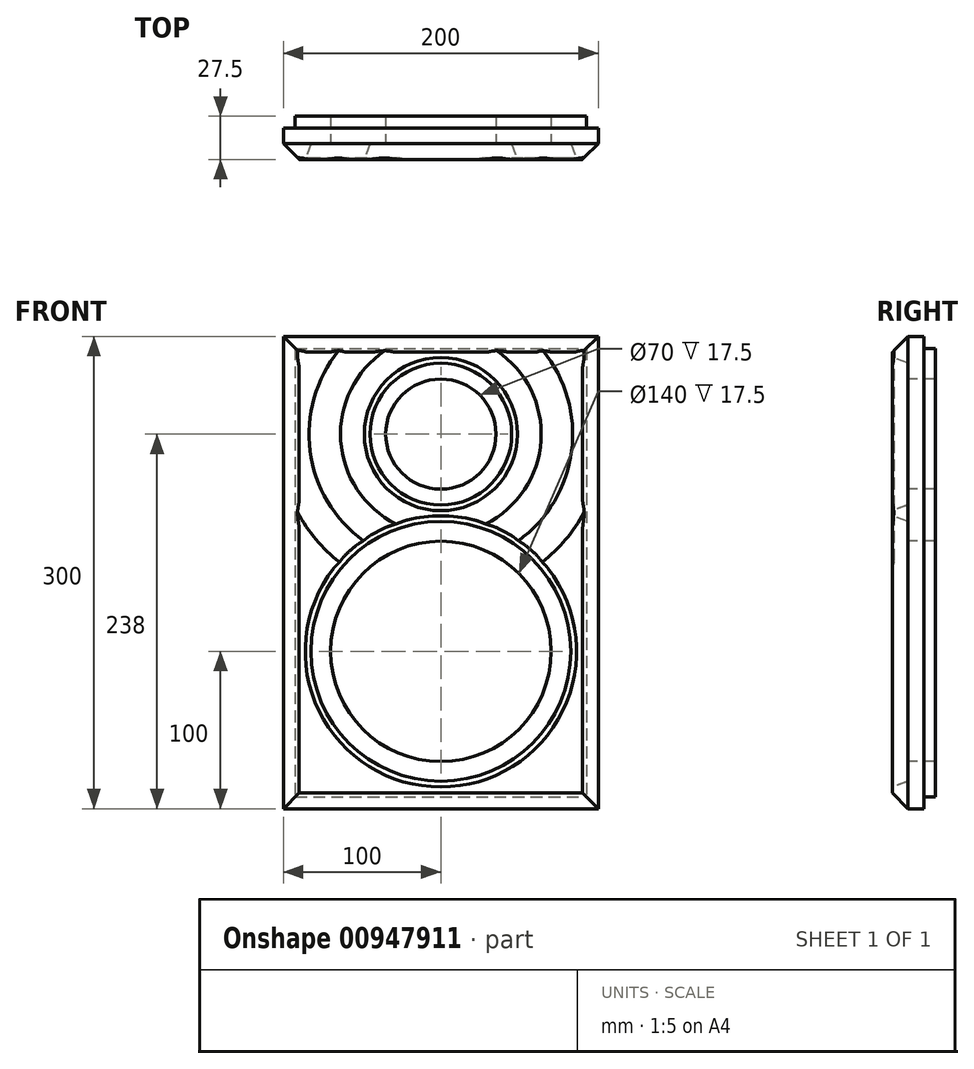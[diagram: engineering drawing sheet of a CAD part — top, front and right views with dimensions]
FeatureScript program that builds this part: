
annotation { "Feature Type Name" : "Feature", "Feature Type Description" : "" }
export const myFeature = defineFeature(function(context is Context, id is Id, definition is map)
    precondition{}
    {
        {
            var Q0;
            Q0=qCreatedBy(makeId("Right.planeOp"),FACE);
            cPlane(context, id + "F0", {"entities" : qUnion([Q0]), "cplaneType" : CPlaneType.OFFSET, "offset" : 100 * mm, "width" : 150 * mm, "height" : 150 * mm});
        }
        {
            var Q0;
            Q0=qCreatedBy(makeId("Right.planeOp"),FACE);
            cPlane(context, id + "F1", {"entities" : qUnion([Q0]), "cplaneType" : CPlaneType.OFFSET, "offset" : 100 * mm, "oppositeDirection" : true, "width" : 150 * mm, "height" : 150 * mm});
        }
        {
            var Q0;
            Q0=qCreatedBy(makeId("Right.planeOp"),FACE);
            cPlane(context, id + "F2", {"entities" : qUnion([Q0]), "cplaneType" : CPlaneType.OFFSET, "offset" : (100 - 7.5) * mm, "width" : 150 * mm, "height" : 150 * mm});
        }
        {
            var Q0;
            Q0=qCreatedBy(makeId("Right.planeOp"),FACE);
            cPlane(context, id + "F3", {"entities" : qUnion([Q0]), "cplaneType" : CPlaneType.OFFSET, "offset" : (100 - 7.5) * mm, "oppositeDirection" : true, "width" : 150 * mm, "height" : 150 * mm});
        }
        {
            var Q0;
            Q0=qCreatedBy(makeId("Top.planeOp"),FACE);
            cPlane(context, id + "F4", {"entities" : qUnion([Q0]), "cplaneType" : CPlaneType.OFFSET, "offset" : 7.7 * mm, "width" : 150 * mm, "height" : 150 * mm});
        }
        {
            var Q0;
            Q0=qCreatedBy(makeId("Top.planeOp"),FACE);
            cPlane(context, id + "F5", {"entities" : qUnion([Q0]), "cplaneType" : CPlaneType.OFFSET, "offset" : 300 * mm, "width" : 150 * mm, "height" : 150 * mm});
        }
        {
            var Q0;
            Q0=qCreatedBy(makeId("Top.planeOp"),FACE);
            cPlane(context, id + "F6", {"entities" : qUnion([Q0]), "cplaneType" : CPlaneType.OFFSET, "offset" : (300 - 7.5) * mm, "width" : 150 * mm, "height" : 150 * mm});
        }
        {
            var Q0;
            Q0=qCreatedBy(makeId("Front.planeOp"),FACE);
            cPlane(context, id + "F7", {"entities" : qUnion([Q0]), "cplaneType" : CPlaneType.OFFSET, "offset" : 150 * mm, "width" : 150 * mm, "height" : 150 * mm});
        }
        {
            var Q0;
            Q0=qCreatedBy(makeId("Front.planeOp"),FACE);
            cPlane(context, id + "F8", {"entities" : qUnion([Q0]), "cplaneType" : CPlaneType.OFFSET, "offset" : (150 - 7.5) * mm, "width" : 150 * mm, "height" : 150 * mm});
        }
        {
            var Q0;
            Q0=qCreatedBy(id+"F8.planeOp",FACE);
            var sketch = newSketch(context, id + "F9", { "sketchPlane" : qUnion([Q0])});
            skLineSegment(sketch, "E0.bottom", {"start": v(-92.5, 292.5) * mm, "end": v(92.5, 292.5) * mm});
            skLineSegment(sketch, "E0.top", {"start": v(-92.5, 7.7) * mm, "end": v(92.5, 7.7) * mm});
            skLineSegment(sketch, "E0.left", {"start": v(-92.5, 292.5) * mm, "end": v(-92.5, 7.7) * mm});
            skLineSegment(sketch, "E0.right", {"start": v(92.5, 292.5) * mm, "end": v(92.5, 7.7) * mm});
            skSolve(sketch);
        }
        {
            var Q0;
            Q0=makeQuery(id+"F9.imprint","IMPRINT",FACE,{"disambiguationData":[TD([[makeQuery(id+"F9.imprint","IMPRINT",EDGE,{"derivedFrom":sQuery(id+"F9.wireOp",EDGE,"E0.bottom")}),-1.0]])]});
            extrude(context, id + "F10", {"entities" : qUnion([Q0]), "depth" : 7.5 * mm, "offsetDistance" : 25 * mm});
        }
        {
            var Q0;
            Q0=qCreatedBy(id+"F7.planeOp",FACE);
            var sketch = newSketch(context, id + "F11", { "sketchPlane" : qUnion([Q0])});
            skLineSegment(sketch, "E1.bottom", {"start": v(-100, 300) * mm, "end": v(100, 300) * mm});
            skLineSegment(sketch, "E1.top", {"start": v(-100, 0) * mm, "end": v(100, 0) * mm});
            skLineSegment(sketch, "E1.left", {"start": v(-100, 300) * mm, "end": v(-100, 0) * mm});
            skLineSegment(sketch, "E1.right", {"start": v(100, 300) * mm, "end": v(100, 0) * mm});
            skSolve(sketch);
        }
        {
            var Q0;
            Q0=makeQuery(id+"F11.imprint","IMPRINT",FACE,{"disambiguationData":[TD([[makeQuery(id+"F11.imprint","IMPRINT",EDGE,{"derivedFrom":sQuery(id+"F11.wireOp",EDGE,"E1.bottom")}),-1.0]])]});
            extrude(context, id + "F12", {"entities" : qUnion([Q0]), "operationType" : NewBodyOperationType.ADD, "depth" : 20 * mm, "offsetDistance" : 25 * mm});
        }
        {
            var Q0;
            Q0=qCreatedBy(id+"F0.planeOp",FACE);
            var sketch = newSketch(context, id + "F13", { "sketchPlane" : qUnion([Q0])});
            skLineSegment(sketch, "E2", {"start": v(-220, 0) * mm, "end": v(-220, 300) * mm});
            skLineSegment(sketch, "E3", {"start": v(-220, 300) * mm, "end": v(-180, 300) * mm});
            skLineSegment(sketch, "E4", {"start": v(-180, 300) * mm, "end": v(-180, 0) * mm});
            skLineSegment(sketch, "E5", {"start": v(-180, 0) * mm, "end": v(-220, 0) * mm});
            skSolve(sketch);
        }
        {
            var Q0;
            Q0=qCreatedBy(makeId("Front.planeOp"),FACE);
            cPlane(context, id + "F14", {"entities" : qUnion([Q0]), "cplaneType" : CPlaneType.OFFSET, "offset" : 300 * mm, "width" : 150 * mm, "height" : 150 * mm});
        }
        {
            var Q0;
            Q0=qCreatedBy(makeId("Front.planeOp"),FACE);
            cPlane(context, id + "F15", {"entities" : qUnion([Q0]), "cplaneType" : CPlaneType.OFFSET, "offset" : 160 * mm, "width" : 150 * mm, "height" : 150 * mm});
        }
        {
            var Q0;
            Q0=qCreatedBy(id+"F14.planeOp",FACE);
            var sketch = newSketch(context, id + "F16", { "sketchPlane" : qUnion([Q0])});
            skCircle(sketch, "E6", {"center": v(0, 100) * mm, "radius": 70 * mm});
            skSolve(sketch);
        }
        {
            var Q0;
            Q0=qSketchRegion(id+"F16",true);
            var Q1;
            Q1=qCreatedBy(id+"F8.planeOp",FACE);
            extrude(context, id + "F17", {"entities" : qUnion([Q0]), "operationType" : NewBodyOperationType.REMOVE, "endBound" : BoundingType.UP_TO_SURFACE, "oppositeDirection" : true, "depth" : 25 * mm, "endBoundEntityFace" : qUnion([Q1]), "offsetDistance" : 25 * mm});
        }
        {
            var Q0;
            Q0=qCreatedBy(id+"F14.planeOp",FACE);
            var sketch = newSketch(context, id + "F18", { "sketchPlane" : qUnion([Q0])});
            skCircle(sketch, "E7", {"center": v(0, 100) * mm, "radius": 82.5 * mm});
            skSolve(sketch);
        }
        {
            var Q0;
            Q0=qSketchRegion(id+"F18",true);
            var Q1;
            Q1=qCreatedBy(id+"F15.planeOp",FACE);
            extrude(context, id + "F19", {"entities" : qUnion([Q0]), "operationType" : NewBodyOperationType.REMOVE, "endBound" : BoundingType.UP_TO_SURFACE, "oppositeDirection" : true, "depth" : 25 * mm, "endBoundEntityFace" : qUnion([Q1]), "offsetDistance" : 25 * mm});
        }
        {
            var Q0;
            Q0=qCreatedBy(id+"F14.planeOp",FACE);
            var sketch = newSketch(context, id + "F20", { "sketchPlane" : qUnion([Q0])});
            skCircle(sketch, "E8", {"center": v(0, 238) * mm, "radius": 35 * mm});
            skSolve(sketch);
        }
        {
            var Q0;
            Q0=makeQuery(id+"F20.imprint","IMPRINT",FACE,{"disambiguationData":[TD([[makeQuery(id+"F20.imprint","IMPRINT",EDGE,{"derivedFrom":sQuery(id+"F20.wireOp",EDGE,"E8")}),1.0]])]});
            var Q1;
            Q1=qCreatedBy(id+"F8.planeOp",FACE);
            extrude(context, id + "F21", {"entities" : qUnion([Q0]), "operationType" : NewBodyOperationType.REMOVE, "endBound" : BoundingType.UP_TO_SURFACE, "oppositeDirection" : true, "depth" : 25 * mm, "endBoundEntityFace" : qUnion([Q1]), "offsetDistance" : 25 * mm});
        }
        {
            var Q0;
            Q0=qCreatedBy(id+"F14.planeOp",FACE);
            var sketch = newSketch(context, id + "F22", { "sketchPlane" : qUnion([Q0])});
            skCircle(sketch, "E9", {"center": v(0, 238) * mm, "radius": 45 * mm});
            skSolve(sketch);
        }
        {
            var Q0;
            Q0=qSketchRegion(id+"F22",true);
            var Q1;
            Q1=qCreatedBy(id+"F15.planeOp",FACE);
            extrude(context, id + "F23", {"entities" : qUnion([Q0]), "operationType" : NewBodyOperationType.REMOVE, "endBound" : BoundingType.UP_TO_SURFACE, "oppositeDirection" : true, "depth" : 25 * mm, "endBoundEntityFace" : qUnion([Q1]), "offsetDistance" : 25 * mm});
        }
        {
            var Q0;
            Q0=makeQuery(id+"F13.imprint","IMPRINT",FACE,{"disambiguationData":[TD([[makeQuery(id+"F13.imprint","IMPRINT",EDGE,{"derivedFrom":sQuery(id+"F13.wireOp",EDGE,"E2")}),-1.0]])]});
            var Q1;
            Q1=qCreatedBy(id+"F1.planeOp",FACE);
            extrude(context, id + "F24", {"entities" : qUnion([Q0]), "operationType" : NewBodyOperationType.REMOVE, "endBound" : BoundingType.UP_TO_SURFACE, "oppositeDirection" : true, "depth" : 25 * mm, "endBoundEntityFace" : qUnion([Q1]), "offsetDistance" : 25 * mm});
        }
        {
            var Q0;
            Q0=makeQuery(id+"F12.opExtrude","CAP_EDGE",EDGE,{"disambiguationData":[OSD([sQuery(id+"F11.wireOp",EDGE,"E1.right")])],"isStart":false});
            var Q1;
            Q1=makeQuery(id+"F12.opExtrude","CAP_EDGE",EDGE,{"disambiguationData":[OSD([sQuery(id+"F11.wireOp",EDGE,"E1.bottom")])],"isStart":false});
            var Q2;
            Q2=makeQuery(id+"F12.opExtrude","CAP_EDGE",EDGE,{"disambiguationData":[OSD([sQuery(id+"F11.wireOp",EDGE,"E1.left")])],"isStart":false});
            var Q3;
            Q3=makeQuery(id+"F12.opExtrude","CAP_EDGE",EDGE,{"disambiguationData":[OSD([sQuery(id+"F11.wireOp",EDGE,"E1.top")])],"isStart":false});
            chamfer(context, id + "F25", {"entities" : qUnion([Q0, Q1, Q2, Q3]), "width" : 10 * mm, "tangentPropagation" : true});
        }
        {
            var Q0;
            Q0=makeQuery(id+"F19.boolean.opBoolean","INTERSECT",EDGE,{"derivedFrom":[makeQuery(id+"F12.opExtrude","CAP_FACE",FACE,{"disambiguationData":[OSD([sQuery(id+"F11.wireOp",EDGE,"E1.bottom"),sQuery(id+"F11.wireOp",EDGE,"E1.top"),sQuery(id+"F11.wireOp",EDGE,"E1.left"),sQuery(id+"F11.wireOp",EDGE,"E1.right")])],"isStart":false}),makeQuery(id+"F19.opExtrude","SWEPT_FACE",FACE,{"disambiguationData":[OSD([sQuery(id+"F18.wireOp",EDGE,"E7")])]})]});
            chamfer(context, id + "F26", {"entities" : qUnion([Q0]), "chamferType" : ChamferType.OFFSET_ANGLE, "width" : 10 * mm, "oppositeDirection" : false, "angle" : 20 * degree, "tangentPropagation" : true});
        }
        {
            var Q0;
            Q0=makeQuery(id+"F23.boolean.opBoolean","INTERSECT",EDGE,{"derivedFrom":[makeQuery(id+"F12.opExtrude","CAP_FACE",FACE,{"disambiguationData":[OSD([sQuery(id+"F11.wireOp",EDGE,"E1.bottom"),sQuery(id+"F11.wireOp",EDGE,"E1.top"),sQuery(id+"F11.wireOp",EDGE,"E1.left"),sQuery(id+"F11.wireOp",EDGE,"E1.right")])],"isStart":false}),makeQuery(id+"F23.opExtrude","SWEPT_FACE",FACE,{"disambiguationData":[OSD([sQuery(id+"F22.wireOp",EDGE,"E9")])]})]});
            chamfer(context, id + "F27", {"entities" : qUnion([Q0]), "chamferType" : ChamferType.OFFSET_ANGLE, "width" : 10 * mm, "oppositeDirection" : false, "angle" : 20 * degree, "tangentPropagation" : true});
        }
        {
            var Q0;
            Q0=qCreatedBy(id+"F14.planeOp",FACE);
            var sketch = newSketch(context, id + "F28", { "sketchPlane" : qUnion([Q0])});
            skCircle(sketch, "E10", {"center": v(0, 238) * mm, "radius": 60 * mm});
            skCircle(sketch, "E11", {"center": v(0, 238) * mm, "radius": 67.5 * mm});
            skCircle(sketch, "E12", {"center": v(0, 238) * mm, "radius": 80 * mm});
            skCircle(sketch, "E13", {"center": v(0, 238) * mm, "radius": 87.5 * mm});
            skCircle(sketch, "E14", {"center": v(0, 238) * mm, "radius": 100 * mm});
            skCircle(sketch, "E15", {"center": v(0, 238) * mm, "radius": 107.5 * mm});
            skSolve(sketch);
        }
        {
            var Q0;
            Q0 = qSketchRegion(id + "F28", true);
            var Q1;
            Q1=makeQuery(id+"F28.imprint","IMPRINT",FACE,{"disambiguationData":[TD([[makeQuery(id+"F28.imprint","IMPRINT",EDGE,{"derivedFrom":sQuery(id+"F28.wireOp",EDGE,"E12")}),-1.0]])]});
            var Q2;
            Q2=makeQuery(id+"F28.imprint","IMPRINT",FACE,{"disambiguationData":[TD([[makeQuery(id+"F28.imprint","IMPRINT",EDGE,{"derivedFrom":sQuery(id+"F28.wireOp",EDGE,"E10")}),-1.0]])]});
            extrude(context, id + "F29", {"entities" : qUnion([Q0, Q1, Q2]), "operationType" : NewBodyOperationType.REMOVE, "oppositeDirection" : true, "depth" : 131 * mm, "offsetDistance" : 25 * mm});
        }
        {
            var Q0;
            Q0=makeQuery(id+"F29.boolean.opBoolean","COPY",EDGE,{"disambiguationData":[OD(1.0)],"derivedFrom":makeQuery(id+"F29.opExtrude","CAP_EDGE",EDGE,{"disambiguationData":[OSD([sQuery(id+"F28.wireOp",EDGE,"E11")])],"isStart":false})});
            var Q1;
            Q1=makeQuery(id+"F29.boolean.opBoolean","COPY",EDGE,{"disambiguationData":[OD(1.0)],"derivedFrom":makeQuery(id+"F29.opExtrude","CAP_EDGE",EDGE,{"disambiguationData":[OSD([sQuery(id+"F28.wireOp",EDGE,"E13")])],"isStart":false})});
            var Q2;
            {var subQ0=sQuery(id+"F11.wireOp",EDGE,"E1.right");var subQ1=sQuery(id+"F28.wireOp",EDGE,"E15");Q2=makeQuery(id+"F29.boolean.opBoolean","COPY",EDGE,{"disambiguationData":[TD([makeQuery(id+"F25.opChamfer","BLEND_FACE",FACE,{"disambiguationData":[OSD([subQ0])]})])],"derivedFrom":makeQuery(id+"F29.opExtrude","CAP_EDGE",EDGE,{"disambiguationData":[OSD([subQ1])],"isStart":false})});}
            var Q3;
            Q3=makeQuery(id+"F29.boolean.opBoolean","COPY",EDGE,{"disambiguationData":[OD(1.0)],"derivedFrom":makeQuery(id+"F29.opExtrude","CAP_EDGE",EDGE,{"disambiguationData":[OSD([sQuery(id+"F28.wireOp",EDGE,"E10")])],"isStart":false})});
            var Q4;
            Q4=makeQuery(id+"F29.boolean.opBoolean","COPY",EDGE,{"disambiguationData":[OD(1.0)],"derivedFrom":makeQuery(id+"F29.opExtrude","CAP_EDGE",EDGE,{"disambiguationData":[OSD([sQuery(id+"F28.wireOp",EDGE,"E12")])],"isStart":false})});
            var Q5;
            {var subQ0=sQuery(id+"F11.wireOp",EDGE,"E1.right");var subQ1=sQuery(id+"F28.wireOp",EDGE,"E14");Q5=makeQuery(id+"F29.boolean.opBoolean","COPY",EDGE,{"disambiguationData":[TD([makeQuery(id+"F25.opChamfer","BLEND_FACE",FACE,{"disambiguationData":[OSD([subQ0])]}),makeQuery(id+"F26.opChamfer","BLEND_FACE",FACE,{"disambiguationData":[OSD([sQuery(id+"F11.wireOp",EDGE,"E1.bottom"),sQuery(id+"F11.wireOp",EDGE,"E1.top"),sQuery(id+"F11.wireOp",EDGE,"E1.left"),subQ0,sQuery(id+"F18.wireOp",EDGE,"E7")])]}),makeQuery(id+"F29.opExtrude","SWEPT_FACE",FACE,{"disambiguationData":[OSD([subQ1])]}),makeQuery(id+"F29.opExtrude","CAP_FACE",FACE,{"disambiguationData":[OSD([subQ1,sQuery(id+"F28.wireOp",EDGE,"E15")])],"isStart":false})])],"derivedFrom":makeQuery(id+"F29.opExtrude","CAP_EDGE",EDGE,{"disambiguationData":[OSD([subQ1])],"isStart":false})});}
            var Q6;
            {var subQ0=sQuery(id+"F28.wireOp",EDGE,"E14");Q6=makeQuery(id+"F29.boolean.opBoolean","COPY",EDGE,{"disambiguationData":[TD([makeQuery(id+"F25.opChamfer","BLEND_FACE",FACE,{"disambiguationData":[OSD([sQuery(id+"F11.wireOp",EDGE,"E1.bottom")])]}),makeQuery(id+"F25.opChamfer","BLEND_FACE",FACE,{"disambiguationData":[OSD([sQuery(id+"F11.wireOp",EDGE,"E1.right")])]}),makeQuery(id+"F29.opExtrude","SWEPT_FACE",FACE,{"disambiguationData":[OSD([subQ0])]}),makeQuery(id+"F29.opExtrude","CAP_FACE",FACE,{"disambiguationData":[OSD([subQ0,sQuery(id+"F28.wireOp",EDGE,"E15")])],"isStart":false})])],"derivedFrom":makeQuery(id+"F29.opExtrude","CAP_EDGE",EDGE,{"disambiguationData":[OSD([subQ0])],"isStart":false})});}
            var Q7;
            Q7=makeQuery(id+"F29.boolean.opBoolean","COPY",EDGE,{"disambiguationData":[OD(0.0)],"derivedFrom":makeQuery(id+"F29.opExtrude","CAP_EDGE",EDGE,{"disambiguationData":[OSD([sQuery(id+"F28.wireOp",EDGE,"E10")])],"isStart":false})});
            var Q8;
            Q8=makeQuery(id+"F29.boolean.opBoolean","COPY",EDGE,{"disambiguationData":[OD(0.0)],"derivedFrom":makeQuery(id+"F29.opExtrude","CAP_EDGE",EDGE,{"disambiguationData":[OSD([sQuery(id+"F28.wireOp",EDGE,"E12")])],"isStart":false})});
            var Q9;
            {var subQ0=sQuery(id+"F11.wireOp",EDGE,"E1.left");var subQ1=sQuery(id+"F28.wireOp",EDGE,"E14");Q9=makeQuery(id+"F29.boolean.opBoolean","COPY",EDGE,{"disambiguationData":[TD([makeQuery(id+"F25.opChamfer","BLEND_FACE",FACE,{"disambiguationData":[OSD([subQ0])]}),makeQuery(id+"F26.opChamfer","BLEND_FACE",FACE,{"disambiguationData":[OSD([sQuery(id+"F11.wireOp",EDGE,"E1.bottom"),sQuery(id+"F11.wireOp",EDGE,"E1.top"),subQ0,sQuery(id+"F11.wireOp",EDGE,"E1.right"),sQuery(id+"F18.wireOp",EDGE,"E7")])]}),makeQuery(id+"F29.opExtrude","SWEPT_FACE",FACE,{"disambiguationData":[OSD([subQ1])]}),makeQuery(id+"F29.opExtrude","CAP_FACE",FACE,{"disambiguationData":[OSD([subQ1,sQuery(id+"F28.wireOp",EDGE,"E15")])],"isStart":false})])],"derivedFrom":makeQuery(id+"F29.opExtrude","CAP_EDGE",EDGE,{"disambiguationData":[OSD([subQ1])],"isStart":false})});}
            var Q10;
            {var subQ0=sQuery(id+"F28.wireOp",EDGE,"E14");Q10=makeQuery(id+"F29.boolean.opBoolean","COPY",EDGE,{"disambiguationData":[TD([makeQuery(id+"F25.opChamfer","BLEND_FACE",FACE,{"disambiguationData":[OSD([sQuery(id+"F11.wireOp",EDGE,"E1.bottom")])]}),makeQuery(id+"F25.opChamfer","BLEND_FACE",FACE,{"disambiguationData":[OSD([sQuery(id+"F11.wireOp",EDGE,"E1.left")])]}),makeQuery(id+"F29.opExtrude","SWEPT_FACE",FACE,{"disambiguationData":[OSD([subQ0])]}),makeQuery(id+"F29.opExtrude","CAP_FACE",FACE,{"disambiguationData":[OSD([subQ0,sQuery(id+"F28.wireOp",EDGE,"E15")])],"isStart":false})])],"derivedFrom":makeQuery(id+"F29.opExtrude","CAP_EDGE",EDGE,{"disambiguationData":[OSD([subQ0])],"isStart":false})});}
            var Q11;
            Q11=makeQuery(id+"F29.boolean.opBoolean","COPY",EDGE,{"disambiguationData":[OD(0.0)],"derivedFrom":makeQuery(id+"F29.opExtrude","CAP_EDGE",EDGE,{"disambiguationData":[OSD([sQuery(id+"F28.wireOp",EDGE,"E13")])],"isStart":false})});
            var Q12;
            Q12=makeQuery(id+"F29.boolean.opBoolean","COPY",EDGE,{"disambiguationData":[OD(0.0)],"derivedFrom":makeQuery(id+"F29.opExtrude","CAP_EDGE",EDGE,{"disambiguationData":[OSD([sQuery(id+"F28.wireOp",EDGE,"E11")])],"isStart":false})});
            var Q13;
            {var subQ0=sQuery(id+"F11.wireOp",EDGE,"E1.left");var subQ1=sQuery(id+"F28.wireOp",EDGE,"E15");Q13=makeQuery(id+"F29.boolean.opBoolean","COPY",EDGE,{"disambiguationData":[TD([makeQuery(id+"F25.opChamfer","BLEND_FACE",FACE,{"disambiguationData":[OSD([subQ0])]})])],"derivedFrom":makeQuery(id+"F29.opExtrude","CAP_EDGE",EDGE,{"disambiguationData":[OSD([subQ1])],"isStart":false})});}
            fillet(context, id + "F30", {"entities" : qUnion([Q0, Q1, Q2, Q3, Q4, Q5, Q6, Q7, Q8, Q9, Q10, Q11, Q12, Q13]), "radius" : 10 * mm, "tangentPropagation" : true, "allowEdgeOverflow" : false});
        }
        {
            var Q0;
            {var subQ0=sQuery(id+"F11.wireOp",EDGE,"E1.bottom");var subQ1=sQuery(id+"F28.wireOp",EDGE,"E10");var subQ2=sQuery(id+"F11.wireOp",EDGE,"E1.right");var subQ3=sQuery(id+"F11.wireOp",EDGE,"E1.left");var subQ4=sQuery(id+"F11.wireOp",EDGE,"E1.top");Q0=makeQuery(id+"F30.opFillet","BLEND_EDGE",EDGE,{"blendedFrom":[makeQuery(id+"F29.boolean.opBoolean","COPY",EDGE,{"disambiguationData":[OD(1.0)],"derivedFrom":makeQuery(id+"F29.opExtrude","CAP_EDGE",EDGE,{"disambiguationData":[OSD([subQ1])],"isStart":false})}),makeQuery(id+"F29.boolean.opBoolean","SPLIT",FACE,{"disambiguationData":[TD([makeQuery(id+"F25.opChamfer","BLEND_FACE",FACE,{"disambiguationData":[OSD([subQ0])]}),makeQuery(id+"F26.opChamfer","BLEND_FACE",FACE,{"disambiguationData":[OSD([subQ0,subQ4,subQ3,subQ2,sQuery(id+"F18.wireOp",EDGE,"E7")])]}),makeQuery(id+"F27.opChamfer","BLEND_FACE",FACE,{"disambiguationData":[OSD([subQ0,subQ4,subQ3,subQ2,sQuery(id+"F22.wireOp",EDGE,"E9")])]}),makeQuery(id+"F29.opExtrude","SWEPT_FACE",FACE,{"disambiguationData":[OSD([subQ1])]})])],"derivedFrom":makeQuery(id+"F12.opExtrude","CAP_FACE",FACE,{"disambiguationData":[OSD([subQ0,subQ4,subQ3,subQ2])],"isStart":false})})],"blendedInto":[makeQuery(id+"F29.boolean.opBoolean","SPLIT",FACE,{"disambiguationData":[TD([makeQuery(id+"F25.opChamfer","BLEND_FACE",FACE,{"disambiguationData":[OSD([subQ0])]}),makeQuery(id+"F26.opChamfer","BLEND_FACE",FACE,{"disambiguationData":[OSD([subQ0,subQ4,subQ3,subQ2,sQuery(id+"F18.wireOp",EDGE,"E7")])]}),makeQuery(id+"F27.opChamfer","BLEND_FACE",FACE,{"disambiguationData":[OSD([subQ0,subQ4,subQ3,subQ2,sQuery(id+"F22.wireOp",EDGE,"E9")])]}),makeQuery(id+"F29.opExtrude","SWEPT_FACE",FACE,{"disambiguationData":[OSD([subQ1])]})])],"derivedFrom":makeQuery(id+"F12.opExtrude","CAP_FACE",FACE,{"disambiguationData":[OSD([subQ0,subQ4,subQ3,subQ2])],"isStart":false})})]});}
            var Q1;
            {var subQ0=sQuery(id+"F11.wireOp",EDGE,"E1.bottom");var subQ1=sQuery(id+"F11.wireOp",EDGE,"E1.right");var subQ2=sQuery(id+"F11.wireOp",EDGE,"E1.left");var subQ3=sQuery(id+"F11.wireOp",EDGE,"E1.top");var subQ4=sQuery(id+"F28.wireOp",EDGE,"E11");Q1=makeQuery(id+"F30.opFillet","BLEND_EDGE",EDGE,{"blendedFrom":[makeQuery(id+"F29.boolean.opBoolean","COPY",EDGE,{"disambiguationData":[OD(1.0)],"derivedFrom":makeQuery(id+"F29.opExtrude","CAP_EDGE",EDGE,{"disambiguationData":[OSD([subQ4])],"isStart":false})}),makeQuery(id+"F29.boolean.opBoolean","SPLIT",FACE,{"disambiguationData":[TD([makeQuery(id+"F25.opChamfer","BLEND_FACE",FACE,{"disambiguationData":[OSD([subQ0])]}),makeQuery(id+"F26.opChamfer","BLEND_FACE",FACE,{"disambiguationData":[OSD([subQ0,subQ3,subQ2,subQ1,sQuery(id+"F18.wireOp",EDGE,"E7")])]}),makeQuery(id+"F29.opExtrude","SWEPT_FACE",FACE,{"disambiguationData":[OSD([subQ4])]}),makeQuery(id+"F29.opExtrude","SWEPT_FACE",FACE,{"disambiguationData":[OSD([sQuery(id+"F28.wireOp",EDGE,"E12")])]})]),OD(1.0)],"derivedFrom":makeQuery(id+"F12.opExtrude","CAP_FACE",FACE,{"disambiguationData":[OSD([subQ0,subQ3,subQ2,subQ1])],"isStart":false})})],"blendedInto":[makeQuery(id+"F29.boolean.opBoolean","SPLIT",FACE,{"disambiguationData":[TD([makeQuery(id+"F25.opChamfer","BLEND_FACE",FACE,{"disambiguationData":[OSD([subQ0])]}),makeQuery(id+"F26.opChamfer","BLEND_FACE",FACE,{"disambiguationData":[OSD([subQ0,subQ3,subQ2,subQ1,sQuery(id+"F18.wireOp",EDGE,"E7")])]}),makeQuery(id+"F29.opExtrude","SWEPT_FACE",FACE,{"disambiguationData":[OSD([subQ4])]}),makeQuery(id+"F29.opExtrude","SWEPT_FACE",FACE,{"disambiguationData":[OSD([sQuery(id+"F28.wireOp",EDGE,"E12")])]})]),OD(1.0)],"derivedFrom":makeQuery(id+"F12.opExtrude","CAP_FACE",FACE,{"disambiguationData":[OSD([subQ0,subQ3,subQ2,subQ1])],"isStart":false})})]});}
            var Q2;
            {var subQ0=sQuery(id+"F11.wireOp",EDGE,"E1.bottom");var subQ1=sQuery(id+"F11.wireOp",EDGE,"E1.right");var subQ2=sQuery(id+"F11.wireOp",EDGE,"E1.left");var subQ3=sQuery(id+"F11.wireOp",EDGE,"E1.top");var subQ4=sQuery(id+"F28.wireOp",EDGE,"E12");Q2=makeQuery(id+"F30.opFillet","BLEND_EDGE",EDGE,{"blendedFrom":[makeQuery(id+"F29.boolean.opBoolean","COPY",EDGE,{"disambiguationData":[OD(1.0)],"derivedFrom":makeQuery(id+"F29.opExtrude","CAP_EDGE",EDGE,{"disambiguationData":[OSD([subQ4])],"isStart":false})}),makeQuery(id+"F29.boolean.opBoolean","SPLIT",FACE,{"disambiguationData":[TD([makeQuery(id+"F25.opChamfer","BLEND_FACE",FACE,{"disambiguationData":[OSD([subQ0])]}),makeQuery(id+"F26.opChamfer","BLEND_FACE",FACE,{"disambiguationData":[OSD([subQ0,subQ3,subQ2,subQ1,sQuery(id+"F18.wireOp",EDGE,"E7")])]}),makeQuery(id+"F29.opExtrude","SWEPT_FACE",FACE,{"disambiguationData":[OSD([sQuery(id+"F28.wireOp",EDGE,"E11")])]}),makeQuery(id+"F29.opExtrude","SWEPT_FACE",FACE,{"disambiguationData":[OSD([subQ4])]})]),OD(1.0)],"derivedFrom":makeQuery(id+"F12.opExtrude","CAP_FACE",FACE,{"disambiguationData":[OSD([subQ0,subQ3,subQ2,subQ1])],"isStart":false})})],"blendedInto":[makeQuery(id+"F29.boolean.opBoolean","SPLIT",FACE,{"disambiguationData":[TD([makeQuery(id+"F25.opChamfer","BLEND_FACE",FACE,{"disambiguationData":[OSD([subQ0])]}),makeQuery(id+"F26.opChamfer","BLEND_FACE",FACE,{"disambiguationData":[OSD([subQ0,subQ3,subQ2,subQ1,sQuery(id+"F18.wireOp",EDGE,"E7")])]}),makeQuery(id+"F29.opExtrude","SWEPT_FACE",FACE,{"disambiguationData":[OSD([sQuery(id+"F28.wireOp",EDGE,"E11")])]}),makeQuery(id+"F29.opExtrude","SWEPT_FACE",FACE,{"disambiguationData":[OSD([subQ4])]})]),OD(1.0)],"derivedFrom":makeQuery(id+"F12.opExtrude","CAP_FACE",FACE,{"disambiguationData":[OSD([subQ0,subQ3,subQ2,subQ1])],"isStart":false})})]});}
            var Q3;
            {var subQ0=sQuery(id+"F28.wireOp",EDGE,"E13");var subQ1=sQuery(id+"F11.wireOp",EDGE,"E1.right");var subQ2=sQuery(id+"F11.wireOp",EDGE,"E1.left");var subQ3=sQuery(id+"F11.wireOp",EDGE,"E1.top");var subQ4=sQuery(id+"F11.wireOp",EDGE,"E1.bottom");Q3=makeQuery(id+"F30.opFillet","BLEND_EDGE",EDGE,{"blendedFrom":[makeQuery(id+"F29.boolean.opBoolean","COPY",EDGE,{"disambiguationData":[OD(1.0)],"derivedFrom":makeQuery(id+"F29.opExtrude","CAP_EDGE",EDGE,{"disambiguationData":[OSD([subQ0])],"isStart":false})}),makeQuery(id+"F29.boolean.opBoolean","SPLIT",FACE,{"disambiguationData":[TD([makeQuery(id+"F25.opChamfer","BLEND_FACE",FACE,{"disambiguationData":[OSD([subQ4])]}),makeQuery(id+"F25.opChamfer","BLEND_FACE",FACE,{"disambiguationData":[OSD([subQ1])]}),makeQuery(id+"F26.opChamfer","BLEND_FACE",FACE,{"disambiguationData":[OSD([subQ4,subQ3,subQ2,subQ1,sQuery(id+"F18.wireOp",EDGE,"E7")])]}),makeQuery(id+"F29.opExtrude","SWEPT_FACE",FACE,{"disambiguationData":[OSD([subQ0])]}),makeQuery(id+"F29.opExtrude","SWEPT_FACE",FACE,{"disambiguationData":[OSD([sQuery(id+"F28.wireOp",EDGE,"E14")])]})])],"derivedFrom":makeQuery(id+"F12.opExtrude","CAP_FACE",FACE,{"disambiguationData":[OSD([subQ4,subQ3,subQ2,subQ1])],"isStart":false})})],"blendedInto":[makeQuery(id+"F29.boolean.opBoolean","SPLIT",FACE,{"disambiguationData":[TD([makeQuery(id+"F25.opChamfer","BLEND_FACE",FACE,{"disambiguationData":[OSD([subQ4])]}),makeQuery(id+"F25.opChamfer","BLEND_FACE",FACE,{"disambiguationData":[OSD([subQ1])]}),makeQuery(id+"F26.opChamfer","BLEND_FACE",FACE,{"disambiguationData":[OSD([subQ4,subQ3,subQ2,subQ1,sQuery(id+"F18.wireOp",EDGE,"E7")])]}),makeQuery(id+"F29.opExtrude","SWEPT_FACE",FACE,{"disambiguationData":[OSD([subQ0])]}),makeQuery(id+"F29.opExtrude","SWEPT_FACE",FACE,{"disambiguationData":[OSD([sQuery(id+"F28.wireOp",EDGE,"E14")])]})])],"derivedFrom":makeQuery(id+"F12.opExtrude","CAP_FACE",FACE,{"disambiguationData":[OSD([subQ4,subQ3,subQ2,subQ1])],"isStart":false})})]});}
            var Q4;
            {var subQ0=sQuery(id+"F11.wireOp",EDGE,"E1.right");var subQ1=sQuery(id+"F11.wireOp",EDGE,"E1.left");var subQ2=sQuery(id+"F11.wireOp",EDGE,"E1.top");var subQ3=sQuery(id+"F11.wireOp",EDGE,"E1.bottom");var subQ4=makeQuery(id+"F26.opChamfer","BLEND_FACE",FACE,{"disambiguationData":[OSD([subQ3,subQ2,subQ1,subQ0,sQuery(id+"F18.wireOp",EDGE,"E7")])]});var subQ5=makeQuery(id+"F25.opChamfer","BLEND_FACE",FACE,{"disambiguationData":[OSD([subQ0])]});var subQ6=sQuery(id+"F28.wireOp",EDGE,"E14");var subQ7=makeQuery(id+"F29.opExtrude","SWEPT_FACE",FACE,{"disambiguationData":[OSD([subQ6])]});Q4=makeQuery(id+"F30.opFillet","BLEND_EDGE",EDGE,{"blendedFrom":[makeQuery(id+"F29.boolean.opBoolean","COPY",EDGE,{"disambiguationData":[TD([subQ5,subQ4,subQ7,makeQuery(id+"F29.opExtrude","CAP_FACE",FACE,{"disambiguationData":[OSD([subQ6,sQuery(id+"F28.wireOp",EDGE,"E15")])],"isStart":false})])],"derivedFrom":makeQuery(id+"F29.opExtrude","CAP_EDGE",EDGE,{"disambiguationData":[OSD([subQ6])],"isStart":false})}),makeQuery(id+"F29.boolean.opBoolean","SPLIT",FACE,{"disambiguationData":[TD([makeQuery(id+"F25.opChamfer","BLEND_FACE",FACE,{"disambiguationData":[OSD([subQ3])]}),subQ5,subQ4,makeQuery(id+"F29.opExtrude","SWEPT_FACE",FACE,{"disambiguationData":[OSD([sQuery(id+"F28.wireOp",EDGE,"E13")])]}),subQ7])],"derivedFrom":makeQuery(id+"F12.opExtrude","CAP_FACE",FACE,{"disambiguationData":[OSD([subQ3,subQ2,subQ1,subQ0])],"isStart":false})})],"blendedInto":[makeQuery(id+"F29.boolean.opBoolean","SPLIT",FACE,{"disambiguationData":[TD([makeQuery(id+"F25.opChamfer","BLEND_FACE",FACE,{"disambiguationData":[OSD([subQ3])]}),subQ5,subQ4,makeQuery(id+"F29.opExtrude","SWEPT_FACE",FACE,{"disambiguationData":[OSD([sQuery(id+"F28.wireOp",EDGE,"E13")])]}),subQ7])],"derivedFrom":makeQuery(id+"F12.opExtrude","CAP_FACE",FACE,{"disambiguationData":[OSD([subQ3,subQ2,subQ1,subQ0])],"isStart":false})})]});}
            var Q5;
            {var subQ0=sQuery(id+"F11.wireOp",EDGE,"E1.right");var subQ1=makeQuery(id+"F25.opChamfer","BLEND_FACE",FACE,{"disambiguationData":[OSD([subQ0])]});var subQ2=sQuery(id+"F11.wireOp",EDGE,"E1.left");var subQ3=sQuery(id+"F11.wireOp",EDGE,"E1.top");var subQ4=sQuery(id+"F11.wireOp",EDGE,"E1.bottom");var subQ5=makeQuery(id+"F26.opChamfer","BLEND_FACE",FACE,{"disambiguationData":[OSD([subQ4,subQ3,subQ2,subQ0,sQuery(id+"F18.wireOp",EDGE,"E7")])]});var subQ6=sQuery(id+"F28.wireOp",EDGE,"E15");var subQ7=makeQuery(id+"F29.opExtrude","SWEPT_FACE",FACE,{"disambiguationData":[OSD([subQ6])]});Q5=makeQuery(id+"F30.opFillet","BLEND_EDGE",EDGE,{"blendedFrom":[makeQuery(id+"F29.boolean.opBoolean","COPY",EDGE,{"disambiguationData":[TD([subQ1])],"derivedFrom":makeQuery(id+"F29.opExtrude","CAP_EDGE",EDGE,{"disambiguationData":[OSD([subQ6])],"isStart":false})}),makeQuery(id+"F29.boolean.opBoolean","SPLIT",FACE,{"disambiguationData":[TD([makeQuery(id+"F25.opChamfer","BLEND_FACE",FACE,{"disambiguationData":[OSD([subQ3])]}),makeQuery(id+"F25.opChamfer","BLEND_FACE",FACE,{"disambiguationData":[OSD([subQ2])]}),subQ1,subQ5,subQ7])],"derivedFrom":makeQuery(id+"F12.opExtrude","CAP_FACE",FACE,{"disambiguationData":[OSD([subQ4,subQ3,subQ2,subQ0])],"isStart":false})})],"blendedInto":[makeQuery(id+"F29.boolean.opBoolean","SPLIT",FACE,{"disambiguationData":[TD([makeQuery(id+"F25.opChamfer","BLEND_FACE",FACE,{"disambiguationData":[OSD([subQ3])]}),makeQuery(id+"F25.opChamfer","BLEND_FACE",FACE,{"disambiguationData":[OSD([subQ2])]}),subQ1,subQ5,subQ7])],"derivedFrom":makeQuery(id+"F12.opExtrude","CAP_FACE",FACE,{"disambiguationData":[OSD([subQ4,subQ3,subQ2,subQ0])],"isStart":false})})]});}
            var Q6;
            {var subQ0=sQuery(id+"F11.wireOp",EDGE,"E1.right");var subQ1=sQuery(id+"F11.wireOp",EDGE,"E1.left");var subQ2=sQuery(id+"F11.wireOp",EDGE,"E1.top");var subQ3=sQuery(id+"F11.wireOp",EDGE,"E1.bottom");var subQ4=makeQuery(id+"F25.opChamfer","BLEND_FACE",FACE,{"disambiguationData":[OSD([subQ0])]});var subQ5=makeQuery(id+"F25.opChamfer","BLEND_FACE",FACE,{"disambiguationData":[OSD([subQ3])]});var subQ6=sQuery(id+"F28.wireOp",EDGE,"E14");var subQ7=makeQuery(id+"F29.opExtrude","SWEPT_FACE",FACE,{"disambiguationData":[OSD([subQ6])]});Q6=makeQuery(id+"F30.opFillet","BLEND_EDGE",EDGE,{"blendedFrom":[makeQuery(id+"F29.boolean.opBoolean","COPY",EDGE,{"disambiguationData":[TD([subQ5,subQ4,subQ7,makeQuery(id+"F29.opExtrude","CAP_FACE",FACE,{"disambiguationData":[OSD([subQ6,sQuery(id+"F28.wireOp",EDGE,"E15")])],"isStart":false})])],"derivedFrom":makeQuery(id+"F29.opExtrude","CAP_EDGE",EDGE,{"disambiguationData":[OSD([subQ6])],"isStart":false})}),makeQuery(id+"F29.boolean.opBoolean","SPLIT",FACE,{"disambiguationData":[TD([subQ5,subQ4,makeQuery(id+"F26.opChamfer","BLEND_FACE",FACE,{"disambiguationData":[OSD([subQ3,subQ2,subQ1,subQ0,sQuery(id+"F18.wireOp",EDGE,"E7")])]}),makeQuery(id+"F29.opExtrude","SWEPT_FACE",FACE,{"disambiguationData":[OSD([sQuery(id+"F28.wireOp",EDGE,"E13")])]}),subQ7])],"derivedFrom":makeQuery(id+"F12.opExtrude","CAP_FACE",FACE,{"disambiguationData":[OSD([subQ3,subQ2,subQ1,subQ0])],"isStart":false})})],"blendedInto":[makeQuery(id+"F29.boolean.opBoolean","SPLIT",FACE,{"disambiguationData":[TD([subQ5,subQ4,makeQuery(id+"F26.opChamfer","BLEND_FACE",FACE,{"disambiguationData":[OSD([subQ3,subQ2,subQ1,subQ0,sQuery(id+"F18.wireOp",EDGE,"E7")])]}),makeQuery(id+"F29.opExtrude","SWEPT_FACE",FACE,{"disambiguationData":[OSD([sQuery(id+"F28.wireOp",EDGE,"E13")])]}),subQ7])],"derivedFrom":makeQuery(id+"F12.opExtrude","CAP_FACE",FACE,{"disambiguationData":[OSD([subQ3,subQ2,subQ1,subQ0])],"isStart":false})})]});}
            var Q7;
            {var subQ0=sQuery(id+"F11.wireOp",EDGE,"E1.bottom");var subQ1=sQuery(id+"F28.wireOp",EDGE,"E10");var subQ2=sQuery(id+"F11.wireOp",EDGE,"E1.right");var subQ3=sQuery(id+"F11.wireOp",EDGE,"E1.left");var subQ4=sQuery(id+"F11.wireOp",EDGE,"E1.top");Q7=makeQuery(id+"F30.opFillet","BLEND_EDGE",EDGE,{"blendedFrom":[makeQuery(id+"F29.boolean.opBoolean","COPY",EDGE,{"disambiguationData":[OD(0.0)],"derivedFrom":makeQuery(id+"F29.opExtrude","CAP_EDGE",EDGE,{"disambiguationData":[OSD([subQ1])],"isStart":false})}),makeQuery(id+"F29.boolean.opBoolean","SPLIT",FACE,{"disambiguationData":[TD([makeQuery(id+"F25.opChamfer","BLEND_FACE",FACE,{"disambiguationData":[OSD([subQ0])]}),makeQuery(id+"F26.opChamfer","BLEND_FACE",FACE,{"disambiguationData":[OSD([subQ0,subQ4,subQ3,subQ2,sQuery(id+"F18.wireOp",EDGE,"E7")])]}),makeQuery(id+"F27.opChamfer","BLEND_FACE",FACE,{"disambiguationData":[OSD([subQ0,subQ4,subQ3,subQ2,sQuery(id+"F22.wireOp",EDGE,"E9")])]}),makeQuery(id+"F29.opExtrude","SWEPT_FACE",FACE,{"disambiguationData":[OSD([subQ1])]})])],"derivedFrom":makeQuery(id+"F12.opExtrude","CAP_FACE",FACE,{"disambiguationData":[OSD([subQ0,subQ4,subQ3,subQ2])],"isStart":false})})],"blendedInto":[makeQuery(id+"F29.boolean.opBoolean","SPLIT",FACE,{"disambiguationData":[TD([makeQuery(id+"F25.opChamfer","BLEND_FACE",FACE,{"disambiguationData":[OSD([subQ0])]}),makeQuery(id+"F26.opChamfer","BLEND_FACE",FACE,{"disambiguationData":[OSD([subQ0,subQ4,subQ3,subQ2,sQuery(id+"F18.wireOp",EDGE,"E7")])]}),makeQuery(id+"F27.opChamfer","BLEND_FACE",FACE,{"disambiguationData":[OSD([subQ0,subQ4,subQ3,subQ2,sQuery(id+"F22.wireOp",EDGE,"E9")])]}),makeQuery(id+"F29.opExtrude","SWEPT_FACE",FACE,{"disambiguationData":[OSD([subQ1])]})])],"derivedFrom":makeQuery(id+"F12.opExtrude","CAP_FACE",FACE,{"disambiguationData":[OSD([subQ0,subQ4,subQ3,subQ2])],"isStart":false})})]});}
            var Q8;
            {var subQ0=sQuery(id+"F11.wireOp",EDGE,"E1.bottom");var subQ1=sQuery(id+"F11.wireOp",EDGE,"E1.right");var subQ2=sQuery(id+"F11.wireOp",EDGE,"E1.left");var subQ3=sQuery(id+"F11.wireOp",EDGE,"E1.top");var subQ4=sQuery(id+"F28.wireOp",EDGE,"E11");Q8=makeQuery(id+"F30.opFillet","BLEND_EDGE",EDGE,{"blendedFrom":[makeQuery(id+"F29.boolean.opBoolean","COPY",EDGE,{"disambiguationData":[OD(0.0)],"derivedFrom":makeQuery(id+"F29.opExtrude","CAP_EDGE",EDGE,{"disambiguationData":[OSD([subQ4])],"isStart":false})}),makeQuery(id+"F29.boolean.opBoolean","SPLIT",FACE,{"disambiguationData":[TD([makeQuery(id+"F25.opChamfer","BLEND_FACE",FACE,{"disambiguationData":[OSD([subQ0])]}),makeQuery(id+"F26.opChamfer","BLEND_FACE",FACE,{"disambiguationData":[OSD([subQ0,subQ3,subQ2,subQ1,sQuery(id+"F18.wireOp",EDGE,"E7")])]}),makeQuery(id+"F29.opExtrude","SWEPT_FACE",FACE,{"disambiguationData":[OSD([subQ4])]}),makeQuery(id+"F29.opExtrude","SWEPT_FACE",FACE,{"disambiguationData":[OSD([sQuery(id+"F28.wireOp",EDGE,"E12")])]})]),OD(0.0)],"derivedFrom":makeQuery(id+"F12.opExtrude","CAP_FACE",FACE,{"disambiguationData":[OSD([subQ0,subQ3,subQ2,subQ1])],"isStart":false})})],"blendedInto":[makeQuery(id+"F29.boolean.opBoolean","SPLIT",FACE,{"disambiguationData":[TD([makeQuery(id+"F25.opChamfer","BLEND_FACE",FACE,{"disambiguationData":[OSD([subQ0])]}),makeQuery(id+"F26.opChamfer","BLEND_FACE",FACE,{"disambiguationData":[OSD([subQ0,subQ3,subQ2,subQ1,sQuery(id+"F18.wireOp",EDGE,"E7")])]}),makeQuery(id+"F29.opExtrude","SWEPT_FACE",FACE,{"disambiguationData":[OSD([subQ4])]}),makeQuery(id+"F29.opExtrude","SWEPT_FACE",FACE,{"disambiguationData":[OSD([sQuery(id+"F28.wireOp",EDGE,"E12")])]})]),OD(0.0)],"derivedFrom":makeQuery(id+"F12.opExtrude","CAP_FACE",FACE,{"disambiguationData":[OSD([subQ0,subQ3,subQ2,subQ1])],"isStart":false})})]});}
            var Q9;
            {var subQ0=sQuery(id+"F11.wireOp",EDGE,"E1.bottom");var subQ1=sQuery(id+"F11.wireOp",EDGE,"E1.right");var subQ2=sQuery(id+"F11.wireOp",EDGE,"E1.left");var subQ3=sQuery(id+"F11.wireOp",EDGE,"E1.top");var subQ4=sQuery(id+"F28.wireOp",EDGE,"E12");Q9=makeQuery(id+"F30.opFillet","BLEND_EDGE",EDGE,{"blendedFrom":[makeQuery(id+"F29.boolean.opBoolean","COPY",EDGE,{"disambiguationData":[OD(0.0)],"derivedFrom":makeQuery(id+"F29.opExtrude","CAP_EDGE",EDGE,{"disambiguationData":[OSD([subQ4])],"isStart":false})}),makeQuery(id+"F29.boolean.opBoolean","SPLIT",FACE,{"disambiguationData":[TD([makeQuery(id+"F25.opChamfer","BLEND_FACE",FACE,{"disambiguationData":[OSD([subQ0])]}),makeQuery(id+"F26.opChamfer","BLEND_FACE",FACE,{"disambiguationData":[OSD([subQ0,subQ3,subQ2,subQ1,sQuery(id+"F18.wireOp",EDGE,"E7")])]}),makeQuery(id+"F29.opExtrude","SWEPT_FACE",FACE,{"disambiguationData":[OSD([sQuery(id+"F28.wireOp",EDGE,"E11")])]}),makeQuery(id+"F29.opExtrude","SWEPT_FACE",FACE,{"disambiguationData":[OSD([subQ4])]})]),OD(0.0)],"derivedFrom":makeQuery(id+"F12.opExtrude","CAP_FACE",FACE,{"disambiguationData":[OSD([subQ0,subQ3,subQ2,subQ1])],"isStart":false})})],"blendedInto":[makeQuery(id+"F29.boolean.opBoolean","SPLIT",FACE,{"disambiguationData":[TD([makeQuery(id+"F25.opChamfer","BLEND_FACE",FACE,{"disambiguationData":[OSD([subQ0])]}),makeQuery(id+"F26.opChamfer","BLEND_FACE",FACE,{"disambiguationData":[OSD([subQ0,subQ3,subQ2,subQ1,sQuery(id+"F18.wireOp",EDGE,"E7")])]}),makeQuery(id+"F29.opExtrude","SWEPT_FACE",FACE,{"disambiguationData":[OSD([sQuery(id+"F28.wireOp",EDGE,"E11")])]}),makeQuery(id+"F29.opExtrude","SWEPT_FACE",FACE,{"disambiguationData":[OSD([subQ4])]})]),OD(0.0)],"derivedFrom":makeQuery(id+"F12.opExtrude","CAP_FACE",FACE,{"disambiguationData":[OSD([subQ0,subQ3,subQ2,subQ1])],"isStart":false})})]});}
            var Q10;
            {var subQ0=sQuery(id+"F11.wireOp",EDGE,"E1.right");var subQ1=sQuery(id+"F11.wireOp",EDGE,"E1.left");var subQ2=sQuery(id+"F11.wireOp",EDGE,"E1.top");var subQ3=sQuery(id+"F11.wireOp",EDGE,"E1.bottom");var subQ4=sQuery(id+"F28.wireOp",EDGE,"E13");Q10=makeQuery(id+"F30.opFillet","BLEND_EDGE",EDGE,{"blendedFrom":[makeQuery(id+"F29.boolean.opBoolean","COPY",EDGE,{"disambiguationData":[OD(0.0)],"derivedFrom":makeQuery(id+"F29.opExtrude","CAP_EDGE",EDGE,{"disambiguationData":[OSD([subQ4])],"isStart":false})}),makeQuery(id+"F29.boolean.opBoolean","SPLIT",FACE,{"disambiguationData":[TD([makeQuery(id+"F25.opChamfer","BLEND_FACE",FACE,{"disambiguationData":[OSD([subQ3])]}),makeQuery(id+"F25.opChamfer","BLEND_FACE",FACE,{"disambiguationData":[OSD([subQ1])]}),makeQuery(id+"F26.opChamfer","BLEND_FACE",FACE,{"disambiguationData":[OSD([subQ3,subQ2,subQ1,subQ0,sQuery(id+"F18.wireOp",EDGE,"E7")])]}),makeQuery(id+"F29.opExtrude","SWEPT_FACE",FACE,{"disambiguationData":[OSD([subQ4])]}),makeQuery(id+"F29.opExtrude","SWEPT_FACE",FACE,{"disambiguationData":[OSD([sQuery(id+"F28.wireOp",EDGE,"E14")])]})])],"derivedFrom":makeQuery(id+"F12.opExtrude","CAP_FACE",FACE,{"disambiguationData":[OSD([subQ3,subQ2,subQ1,subQ0])],"isStart":false})})],"blendedInto":[makeQuery(id+"F29.boolean.opBoolean","SPLIT",FACE,{"disambiguationData":[TD([makeQuery(id+"F25.opChamfer","BLEND_FACE",FACE,{"disambiguationData":[OSD([subQ3])]}),makeQuery(id+"F25.opChamfer","BLEND_FACE",FACE,{"disambiguationData":[OSD([subQ1])]}),makeQuery(id+"F26.opChamfer","BLEND_FACE",FACE,{"disambiguationData":[OSD([subQ3,subQ2,subQ1,subQ0,sQuery(id+"F18.wireOp",EDGE,"E7")])]}),makeQuery(id+"F29.opExtrude","SWEPT_FACE",FACE,{"disambiguationData":[OSD([subQ4])]}),makeQuery(id+"F29.opExtrude","SWEPT_FACE",FACE,{"disambiguationData":[OSD([sQuery(id+"F28.wireOp",EDGE,"E14")])]})])],"derivedFrom":makeQuery(id+"F12.opExtrude","CAP_FACE",FACE,{"disambiguationData":[OSD([subQ3,subQ2,subQ1,subQ0])],"isStart":false})})]});}
            var Q11;
            {var subQ0=sQuery(id+"F11.wireOp",EDGE,"E1.right");var subQ1=sQuery(id+"F11.wireOp",EDGE,"E1.left");var subQ2=sQuery(id+"F11.wireOp",EDGE,"E1.top");var subQ3=sQuery(id+"F11.wireOp",EDGE,"E1.bottom");var subQ4=makeQuery(id+"F26.opChamfer","BLEND_FACE",FACE,{"disambiguationData":[OSD([subQ3,subQ2,subQ1,subQ0,sQuery(id+"F18.wireOp",EDGE,"E7")])]});var subQ5=makeQuery(id+"F25.opChamfer","BLEND_FACE",FACE,{"disambiguationData":[OSD([subQ1])]});var subQ6=sQuery(id+"F28.wireOp",EDGE,"E14");var subQ7=makeQuery(id+"F29.opExtrude","SWEPT_FACE",FACE,{"disambiguationData":[OSD([subQ6])]});Q11=makeQuery(id+"F30.opFillet","BLEND_EDGE",EDGE,{"blendedFrom":[makeQuery(id+"F29.boolean.opBoolean","COPY",EDGE,{"disambiguationData":[TD([subQ5,subQ4,subQ7,makeQuery(id+"F29.opExtrude","CAP_FACE",FACE,{"disambiguationData":[OSD([subQ6,sQuery(id+"F28.wireOp",EDGE,"E15")])],"isStart":false})])],"derivedFrom":makeQuery(id+"F29.opExtrude","CAP_EDGE",EDGE,{"disambiguationData":[OSD([subQ6])],"isStart":false})}),makeQuery(id+"F29.boolean.opBoolean","SPLIT",FACE,{"disambiguationData":[TD([makeQuery(id+"F25.opChamfer","BLEND_FACE",FACE,{"disambiguationData":[OSD([subQ3])]}),subQ5,subQ4,makeQuery(id+"F29.opExtrude","SWEPT_FACE",FACE,{"disambiguationData":[OSD([sQuery(id+"F28.wireOp",EDGE,"E13")])]}),subQ7])],"derivedFrom":makeQuery(id+"F12.opExtrude","CAP_FACE",FACE,{"disambiguationData":[OSD([subQ3,subQ2,subQ1,subQ0])],"isStart":false})})],"blendedInto":[makeQuery(id+"F29.boolean.opBoolean","SPLIT",FACE,{"disambiguationData":[TD([makeQuery(id+"F25.opChamfer","BLEND_FACE",FACE,{"disambiguationData":[OSD([subQ3])]}),subQ5,subQ4,makeQuery(id+"F29.opExtrude","SWEPT_FACE",FACE,{"disambiguationData":[OSD([sQuery(id+"F28.wireOp",EDGE,"E13")])]}),subQ7])],"derivedFrom":makeQuery(id+"F12.opExtrude","CAP_FACE",FACE,{"disambiguationData":[OSD([subQ3,subQ2,subQ1,subQ0])],"isStart":false})})]});}
            var Q12;
            {var subQ0=sQuery(id+"F11.wireOp",EDGE,"E1.right");var subQ1=sQuery(id+"F11.wireOp",EDGE,"E1.left");var subQ2=makeQuery(id+"F25.opChamfer","BLEND_FACE",FACE,{"disambiguationData":[OSD([subQ1])]});var subQ3=sQuery(id+"F11.wireOp",EDGE,"E1.top");var subQ4=sQuery(id+"F11.wireOp",EDGE,"E1.bottom");var subQ5=makeQuery(id+"F26.opChamfer","BLEND_FACE",FACE,{"disambiguationData":[OSD([subQ4,subQ3,subQ1,subQ0,sQuery(id+"F18.wireOp",EDGE,"E7")])]});var subQ6=sQuery(id+"F28.wireOp",EDGE,"E15");var subQ7=makeQuery(id+"F29.opExtrude","SWEPT_FACE",FACE,{"disambiguationData":[OSD([subQ6])]});Q12=makeQuery(id+"F30.opFillet","BLEND_EDGE",EDGE,{"blendedFrom":[makeQuery(id+"F29.boolean.opBoolean","COPY",EDGE,{"disambiguationData":[TD([subQ2])],"derivedFrom":makeQuery(id+"F29.opExtrude","CAP_EDGE",EDGE,{"disambiguationData":[OSD([subQ6])],"isStart":false})}),makeQuery(id+"F29.boolean.opBoolean","SPLIT",FACE,{"disambiguationData":[TD([makeQuery(id+"F25.opChamfer","BLEND_FACE",FACE,{"disambiguationData":[OSD([subQ3])]}),subQ2,makeQuery(id+"F25.opChamfer","BLEND_FACE",FACE,{"disambiguationData":[OSD([subQ0])]}),subQ5,subQ7])],"derivedFrom":makeQuery(id+"F12.opExtrude","CAP_FACE",FACE,{"disambiguationData":[OSD([subQ4,subQ3,subQ1,subQ0])],"isStart":false})})],"blendedInto":[makeQuery(id+"F29.boolean.opBoolean","SPLIT",FACE,{"disambiguationData":[TD([makeQuery(id+"F25.opChamfer","BLEND_FACE",FACE,{"disambiguationData":[OSD([subQ3])]}),subQ2,makeQuery(id+"F25.opChamfer","BLEND_FACE",FACE,{"disambiguationData":[OSD([subQ0])]}),subQ5,subQ7])],"derivedFrom":makeQuery(id+"F12.opExtrude","CAP_FACE",FACE,{"disambiguationData":[OSD([subQ4,subQ3,subQ1,subQ0])],"isStart":false})})]});}
            var Q13;
            {var subQ0=sQuery(id+"F11.wireOp",EDGE,"E1.right");var subQ1=sQuery(id+"F11.wireOp",EDGE,"E1.left");var subQ2=sQuery(id+"F11.wireOp",EDGE,"E1.top");var subQ3=sQuery(id+"F11.wireOp",EDGE,"E1.bottom");var subQ4=makeQuery(id+"F25.opChamfer","BLEND_FACE",FACE,{"disambiguationData":[OSD([subQ1])]});var subQ5=makeQuery(id+"F25.opChamfer","BLEND_FACE",FACE,{"disambiguationData":[OSD([subQ3])]});var subQ6=sQuery(id+"F28.wireOp",EDGE,"E14");var subQ7=makeQuery(id+"F29.opExtrude","SWEPT_FACE",FACE,{"disambiguationData":[OSD([subQ6])]});Q13=makeQuery(id+"F30.opFillet","BLEND_EDGE",EDGE,{"blendedFrom":[makeQuery(id+"F29.boolean.opBoolean","COPY",EDGE,{"disambiguationData":[TD([subQ5,subQ4,subQ7,makeQuery(id+"F29.opExtrude","CAP_FACE",FACE,{"disambiguationData":[OSD([subQ6,sQuery(id+"F28.wireOp",EDGE,"E15")])],"isStart":false})])],"derivedFrom":makeQuery(id+"F29.opExtrude","CAP_EDGE",EDGE,{"disambiguationData":[OSD([subQ6])],"isStart":false})}),makeQuery(id+"F29.boolean.opBoolean","SPLIT",FACE,{"disambiguationData":[TD([subQ5,subQ4,makeQuery(id+"F26.opChamfer","BLEND_FACE",FACE,{"disambiguationData":[OSD([subQ3,subQ2,subQ1,subQ0,sQuery(id+"F18.wireOp",EDGE,"E7")])]}),makeQuery(id+"F29.opExtrude","SWEPT_FACE",FACE,{"disambiguationData":[OSD([sQuery(id+"F28.wireOp",EDGE,"E13")])]}),subQ7])],"derivedFrom":makeQuery(id+"F12.opExtrude","CAP_FACE",FACE,{"disambiguationData":[OSD([subQ3,subQ2,subQ1,subQ0])],"isStart":false})})],"blendedInto":[makeQuery(id+"F29.boolean.opBoolean","SPLIT",FACE,{"disambiguationData":[TD([subQ5,subQ4,makeQuery(id+"F26.opChamfer","BLEND_FACE",FACE,{"disambiguationData":[OSD([subQ3,subQ2,subQ1,subQ0,sQuery(id+"F18.wireOp",EDGE,"E7")])]}),makeQuery(id+"F29.opExtrude","SWEPT_FACE",FACE,{"disambiguationData":[OSD([sQuery(id+"F28.wireOp",EDGE,"E13")])]}),subQ7])],"derivedFrom":makeQuery(id+"F12.opExtrude","CAP_FACE",FACE,{"disambiguationData":[OSD([subQ3,subQ2,subQ1,subQ0])],"isStart":false})})]});}
            fillet(context, id + "F31", {"entities" : qUnion([Q0, Q1, Q2, Q3, Q4, Q5, Q6, Q7, Q8, Q9, Q10, Q11, Q12, Q13]), "radius" : 8 * mm, "tangentPropagation" : true, "allowEdgeOverflow" : false});
        }
    });
